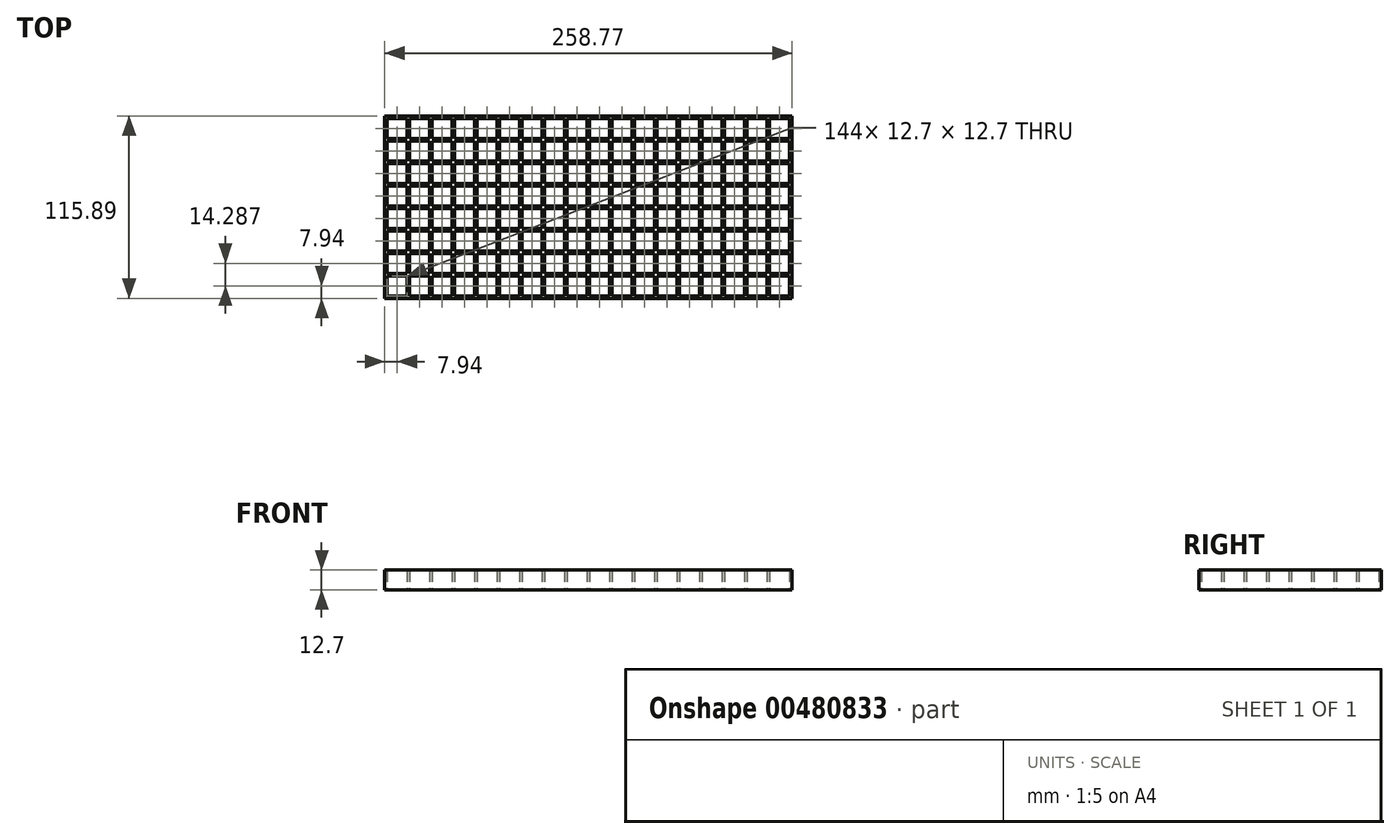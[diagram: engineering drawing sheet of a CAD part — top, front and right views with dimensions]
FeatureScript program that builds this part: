
annotation { "Feature Type Name" : "Feature", "Feature Type Description" : "" }
export const myFeature = defineFeature(function(context is Context, id is Id, definition is map)
    precondition{}
    {
        {
            var Q0;
            Q0=qCreatedBy(makeId("Top.planeOp"),FACE);
            var sketch = newSketch(context, id + "F0", { "sketchPlane" : qUnion([Q0])});
            skLineSegment(sketch, "E0.bottom", {"start": v(0, 0) * mm, "end": v(12.7, 0) * mm});
            skLineSegment(sketch, "E0.top", {"start": v(0, 12.7) * mm, "end": v(12.7, 12.7) * mm});
            skLineSegment(sketch, "E0.left", {"start": v(0, 0) * mm, "end": v(0, 12.7) * mm});
            skLineSegment(sketch, "E0.right", {"start": v(12.7, 0) * mm, "end": v(12.7, 12.7) * mm});
            skLineSegment(sketch, "E1.0.1.0", {"start": v(0, 14.29) * mm, "end": v(12.7, 14.29) * mm});
            skLineSegment(sketch, "E1.0.1.1", {"start": v(0, 26.99) * mm, "end": v(12.7, 26.99) * mm});
            skLineSegment(sketch, "E1.0.1.2", {"start": v(0, 14.29) * mm, "end": v(0, 26.99) * mm});
            skLineSegment(sketch, "E1.0.1.3", {"start": v(12.7, 14.29) * mm, "end": v(12.7, 26.99) * mm});
            skLineSegment(sketch, "E1.0.2.0", {"start": v(0, 28.58) * mm, "end": v(12.7, 28.58) * mm});
            skLineSegment(sketch, "E1.0.2.1", {"start": v(0, 41.28) * mm, "end": v(12.7, 41.28) * mm});
            skLineSegment(sketch, "E1.0.2.2", {"start": v(0, 28.57) * mm, "end": v(0, 41.27) * mm});
            skLineSegment(sketch, "E1.0.2.3", {"start": v(12.7, 28.57) * mm, "end": v(12.7, 41.27) * mm});
            skLineSegment(sketch, "E1.0.3.0", {"start": v(0, 42.86) * mm, "end": v(12.7, 42.86) * mm});
            skLineSegment(sketch, "E1.0.3.1", {"start": v(0, 55.56) * mm, "end": v(12.7, 55.56) * mm});
            skLineSegment(sketch, "E1.0.3.2", {"start": v(0, 42.86) * mm, "end": v(0, 55.56) * mm});
            skLineSegment(sketch, "E1.0.3.3", {"start": v(12.7, 42.86) * mm, "end": v(12.7, 55.56) * mm});
            skLineSegment(sketch, "E1.0.4.0", {"start": v(0, 57.15) * mm, "end": v(12.7, 57.15) * mm});
            skLineSegment(sketch, "E1.0.4.1", {"start": v(0, 69.85) * mm, "end": v(12.7, 69.85) * mm});
            skLineSegment(sketch, "E1.0.4.2", {"start": v(0, 57.15) * mm, "end": v(0, 69.85) * mm});
            skLineSegment(sketch, "E1.0.4.3", {"start": v(12.7, 57.15) * mm, "end": v(12.7, 69.85) * mm});
            skLineSegment(sketch, "E1.0.5.0", {"start": v(0, 71.44) * mm, "end": v(12.7, 71.44) * mm});
            skLineSegment(sketch, "E1.0.5.1", {"start": v(0, 84.14) * mm, "end": v(12.7, 84.14) * mm});
            skLineSegment(sketch, "E1.0.5.2", {"start": v(0, 71.44) * mm, "end": v(0, 84.14) * mm});
            skLineSegment(sketch, "E1.0.5.3", {"start": v(12.7, 71.44) * mm, "end": v(12.7, 84.14) * mm});
            skLineSegment(sketch, "E1.0.6.0", {"start": v(0, 85.73) * mm, "end": v(12.7, 85.73) * mm});
            skLineSegment(sketch, "E1.0.6.1", {"start": v(0, 98.43) * mm, "end": v(12.7, 98.43) * mm});
            skLineSegment(sketch, "E1.0.6.2", {"start": v(0, 85.73) * mm, "end": v(0, 98.43) * mm});
            skLineSegment(sketch, "E1.0.6.3", {"start": v(12.7, 85.73) * mm, "end": v(12.7, 98.43) * mm});
            skLineSegment(sketch, "E1.0.7.0", {"start": v(0, 100.01) * mm, "end": v(12.7, 100.01) * mm});
            skLineSegment(sketch, "E1.0.7.1", {"start": v(0, 112.71) * mm, "end": v(12.7, 112.71) * mm});
            skLineSegment(sketch, "E1.0.7.2", {"start": v(0, 100.01) * mm, "end": v(0, 112.71) * mm});
            skLineSegment(sketch, "E1.0.7.3", {"start": v(12.7, 100.01) * mm, "end": v(12.7, 112.71) * mm});
            skLineSegment(sketch, "E1.1.0.0", {"start": v(14.29, 0) * mm, "end": v(26.99, 0) * mm});
            skLineSegment(sketch, "E1.1.0.1", {"start": v(14.29, 12.7) * mm, "end": v(26.99, 12.7) * mm});
            skLineSegment(sketch, "E1.1.0.2", {"start": v(14.29, 0) * mm, "end": v(14.29, 12.7) * mm});
            skLineSegment(sketch, "E1.1.0.3", {"start": v(26.99, 0) * mm, "end": v(26.99, 12.7) * mm});
            skLineSegment(sketch, "E1.1.1.0", {"start": v(14.29, 14.29) * mm, "end": v(26.99, 14.29) * mm});
            skLineSegment(sketch, "E1.1.1.1", {"start": v(14.29, 26.99) * mm, "end": v(26.99, 26.99) * mm});
            skLineSegment(sketch, "E1.1.1.2", {"start": v(14.29, 14.29) * mm, "end": v(14.29, 26.99) * mm});
            skLineSegment(sketch, "E1.1.1.3", {"start": v(26.99, 14.29) * mm, "end": v(26.99, 26.99) * mm});
            skLineSegment(sketch, "E1.1.2.0", {"start": v(14.29, 28.58) * mm, "end": v(26.99, 28.58) * mm});
            skLineSegment(sketch, "E1.1.2.1", {"start": v(14.29, 41.28) * mm, "end": v(26.99, 41.28) * mm});
            skLineSegment(sketch, "E1.1.2.2", {"start": v(14.29, 28.57) * mm, "end": v(14.29, 41.27) * mm});
            skLineSegment(sketch, "E1.1.2.3", {"start": v(26.99, 28.57) * mm, "end": v(26.99, 41.27) * mm});
            skLineSegment(sketch, "E1.1.3.0", {"start": v(14.29, 42.86) * mm, "end": v(26.99, 42.86) * mm});
            skLineSegment(sketch, "E1.1.3.1", {"start": v(14.29, 55.56) * mm, "end": v(26.99, 55.56) * mm});
            skLineSegment(sketch, "E1.1.3.2", {"start": v(14.29, 42.86) * mm, "end": v(14.29, 55.56) * mm});
            skLineSegment(sketch, "E1.1.3.3", {"start": v(26.99, 42.86) * mm, "end": v(26.99, 55.56) * mm});
            skLineSegment(sketch, "E1.1.4.0", {"start": v(14.29, 57.15) * mm, "end": v(26.99, 57.15) * mm});
            skLineSegment(sketch, "E1.1.4.1", {"start": v(14.29, 69.85) * mm, "end": v(26.99, 69.85) * mm});
            skLineSegment(sketch, "E1.1.4.2", {"start": v(14.29, 57.15) * mm, "end": v(14.29, 69.85) * mm});
            skLineSegment(sketch, "E1.1.4.3", {"start": v(26.99, 57.15) * mm, "end": v(26.99, 69.85) * mm});
            skLineSegment(sketch, "E1.1.5.0", {"start": v(14.29, 71.44) * mm, "end": v(26.99, 71.44) * mm});
            skLineSegment(sketch, "E1.1.5.1", {"start": v(14.29, 84.14) * mm, "end": v(26.99, 84.14) * mm});
            skLineSegment(sketch, "E1.1.5.2", {"start": v(14.29, 71.44) * mm, "end": v(14.29, 84.14) * mm});
            skLineSegment(sketch, "E1.1.5.3", {"start": v(26.99, 71.44) * mm, "end": v(26.99, 84.14) * mm});
            skLineSegment(sketch, "E1.1.6.0", {"start": v(14.29, 85.73) * mm, "end": v(26.99, 85.73) * mm});
            skLineSegment(sketch, "E1.1.6.1", {"start": v(14.29, 98.43) * mm, "end": v(26.99, 98.43) * mm});
            skLineSegment(sketch, "E1.1.6.2", {"start": v(14.29, 85.73) * mm, "end": v(14.29, 98.43) * mm});
            skLineSegment(sketch, "E1.1.6.3", {"start": v(26.99, 85.73) * mm, "end": v(26.99, 98.43) * mm});
            skLineSegment(sketch, "E1.1.7.0", {"start": v(14.29, 100.01) * mm, "end": v(26.99, 100.01) * mm});
            skLineSegment(sketch, "E1.1.7.1", {"start": v(14.29, 112.71) * mm, "end": v(26.99, 112.71) * mm});
            skLineSegment(sketch, "E1.1.7.2", {"start": v(14.29, 100.01) * mm, "end": v(14.29, 112.71) * mm});
            skLineSegment(sketch, "E1.1.7.3", {"start": v(26.99, 100.01) * mm, "end": v(26.99, 112.71) * mm});
            skLineSegment(sketch, "E1.2.0.0", {"start": v(28.58, 0) * mm, "end": v(41.28, 0) * mm});
            skLineSegment(sketch, "E1.2.0.1", {"start": v(28.58, 12.7) * mm, "end": v(41.27, 12.7) * mm});
            skLineSegment(sketch, "E1.2.0.2", {"start": v(28.58, 0) * mm, "end": v(28.58, 12.7) * mm});
            skLineSegment(sketch, "E1.2.0.3", {"start": v(41.28, 0) * mm, "end": v(41.28, 12.7) * mm});
            skLineSegment(sketch, "E1.2.1.0", {"start": v(28.58, 14.29) * mm, "end": v(41.28, 14.29) * mm});
            skLineSegment(sketch, "E1.2.1.1", {"start": v(28.58, 26.99) * mm, "end": v(41.27, 26.99) * mm});
            skLineSegment(sketch, "E1.2.1.2", {"start": v(28.58, 14.29) * mm, "end": v(28.58, 26.99) * mm});
            skLineSegment(sketch, "E1.2.1.3", {"start": v(41.28, 14.29) * mm, "end": v(41.28, 26.99) * mm});
            skLineSegment(sketch, "E1.2.2.0", {"start": v(28.58, 28.58) * mm, "end": v(41.28, 28.58) * mm});
            skLineSegment(sketch, "E1.2.2.1", {"start": v(28.58, 41.28) * mm, "end": v(41.27, 41.28) * mm});
            skLineSegment(sketch, "E1.2.2.2", {"start": v(28.58, 28.57) * mm, "end": v(28.58, 41.27) * mm});
            skLineSegment(sketch, "E1.2.2.3", {"start": v(41.28, 28.57) * mm, "end": v(41.28, 41.27) * mm});
            skLineSegment(sketch, "E1.2.3.0", {"start": v(28.58, 42.86) * mm, "end": v(41.28, 42.86) * mm});
            skLineSegment(sketch, "E1.2.3.1", {"start": v(28.58, 55.56) * mm, "end": v(41.27, 55.56) * mm});
            skLineSegment(sketch, "E1.2.3.2", {"start": v(28.58, 42.86) * mm, "end": v(28.58, 55.56) * mm});
            skLineSegment(sketch, "E1.2.3.3", {"start": v(41.28, 42.86) * mm, "end": v(41.28, 55.56) * mm});
            skLineSegment(sketch, "E1.2.4.0", {"start": v(28.58, 57.15) * mm, "end": v(41.28, 57.15) * mm});
            skLineSegment(sketch, "E1.2.4.1", {"start": v(28.58, 69.85) * mm, "end": v(41.27, 69.85) * mm});
            skLineSegment(sketch, "E1.2.4.2", {"start": v(28.58, 57.15) * mm, "end": v(28.58, 69.85) * mm});
            skLineSegment(sketch, "E1.2.4.3", {"start": v(41.28, 57.15) * mm, "end": v(41.28, 69.85) * mm});
            skLineSegment(sketch, "E1.2.5.0", {"start": v(28.58, 71.44) * mm, "end": v(41.28, 71.44) * mm});
            skLineSegment(sketch, "E1.2.5.1", {"start": v(28.58, 84.14) * mm, "end": v(41.27, 84.14) * mm});
            skLineSegment(sketch, "E1.2.5.2", {"start": v(28.58, 71.44) * mm, "end": v(28.58, 84.14) * mm});
            skLineSegment(sketch, "E1.2.5.3", {"start": v(41.28, 71.44) * mm, "end": v(41.28, 84.14) * mm});
            skLineSegment(sketch, "E1.2.6.0", {"start": v(28.58, 85.73) * mm, "end": v(41.28, 85.73) * mm});
            skLineSegment(sketch, "E1.2.6.1", {"start": v(28.58, 98.43) * mm, "end": v(41.27, 98.43) * mm});
            skLineSegment(sketch, "E1.2.6.2", {"start": v(28.58, 85.73) * mm, "end": v(28.58, 98.43) * mm});
            skLineSegment(sketch, "E1.2.6.3", {"start": v(41.28, 85.73) * mm, "end": v(41.28, 98.43) * mm});
            skLineSegment(sketch, "E1.2.7.0", {"start": v(28.58, 100.01) * mm, "end": v(41.28, 100.01) * mm});
            skLineSegment(sketch, "E1.2.7.1", {"start": v(28.58, 112.71) * mm, "end": v(41.27, 112.71) * mm});
            skLineSegment(sketch, "E1.2.7.2", {"start": v(28.58, 100.01) * mm, "end": v(28.58, 112.71) * mm});
            skLineSegment(sketch, "E1.2.7.3", {"start": v(41.28, 100.01) * mm, "end": v(41.28, 112.71) * mm});
            skLineSegment(sketch, "E1.3.0.0", {"start": v(42.86, 0) * mm, "end": v(55.56, 0) * mm});
            skLineSegment(sketch, "E1.3.0.1", {"start": v(42.86, 12.7) * mm, "end": v(55.56, 12.7) * mm});
            skLineSegment(sketch, "E1.3.0.2", {"start": v(42.86, 0) * mm, "end": v(42.86, 12.7) * mm});
            skLineSegment(sketch, "E1.3.0.3", {"start": v(55.56, 0) * mm, "end": v(55.56, 12.7) * mm});
            skLineSegment(sketch, "E1.3.1.0", {"start": v(42.86, 14.29) * mm, "end": v(55.56, 14.29) * mm});
            skLineSegment(sketch, "E1.3.1.1", {"start": v(42.86, 26.99) * mm, "end": v(55.56, 26.99) * mm});
            skLineSegment(sketch, "E1.3.1.2", {"start": v(42.86, 14.29) * mm, "end": v(42.86, 26.99) * mm});
            skLineSegment(sketch, "E1.3.1.3", {"start": v(55.56, 14.29) * mm, "end": v(55.56, 26.99) * mm});
            skLineSegment(sketch, "E1.3.2.0", {"start": v(42.86, 28.58) * mm, "end": v(55.56, 28.58) * mm});
            skLineSegment(sketch, "E1.3.2.1", {"start": v(42.86, 41.28) * mm, "end": v(55.56, 41.28) * mm});
            skLineSegment(sketch, "E1.3.2.2", {"start": v(42.86, 28.57) * mm, "end": v(42.86, 41.27) * mm});
            skLineSegment(sketch, "E1.3.2.3", {"start": v(55.56, 28.57) * mm, "end": v(55.56, 41.27) * mm});
            skLineSegment(sketch, "E1.3.3.0", {"start": v(42.86, 42.86) * mm, "end": v(55.56, 42.86) * mm});
            skLineSegment(sketch, "E1.3.3.1", {"start": v(42.86, 55.56) * mm, "end": v(55.56, 55.56) * mm});
            skLineSegment(sketch, "E1.3.3.2", {"start": v(42.86, 42.86) * mm, "end": v(42.86, 55.56) * mm});
            skLineSegment(sketch, "E1.3.3.3", {"start": v(55.56, 42.86) * mm, "end": v(55.56, 55.56) * mm});
            skLineSegment(sketch, "E1.3.4.0", {"start": v(42.86, 57.15) * mm, "end": v(55.56, 57.15) * mm});
            skLineSegment(sketch, "E1.3.4.1", {"start": v(42.86, 69.85) * mm, "end": v(55.56, 69.85) * mm});
            skLineSegment(sketch, "E1.3.4.2", {"start": v(42.86, 57.15) * mm, "end": v(42.86, 69.85) * mm});
            skLineSegment(sketch, "E1.3.4.3", {"start": v(55.56, 57.15) * mm, "end": v(55.56, 69.85) * mm});
            skLineSegment(sketch, "E1.3.5.0", {"start": v(42.86, 71.44) * mm, "end": v(55.56, 71.44) * mm});
            skLineSegment(sketch, "E1.3.5.1", {"start": v(42.86, 84.14) * mm, "end": v(55.56, 84.14) * mm});
            skLineSegment(sketch, "E1.3.5.2", {"start": v(42.86, 71.44) * mm, "end": v(42.86, 84.14) * mm});
            skLineSegment(sketch, "E1.3.5.3", {"start": v(55.56, 71.44) * mm, "end": v(55.56, 84.14) * mm});
            skLineSegment(sketch, "E1.3.6.0", {"start": v(42.86, 85.73) * mm, "end": v(55.56, 85.73) * mm});
            skLineSegment(sketch, "E1.3.6.1", {"start": v(42.86, 98.43) * mm, "end": v(55.56, 98.43) * mm});
            skLineSegment(sketch, "E1.3.6.2", {"start": v(42.86, 85.73) * mm, "end": v(42.86, 98.43) * mm});
            skLineSegment(sketch, "E1.3.6.3", {"start": v(55.56, 85.73) * mm, "end": v(55.56, 98.43) * mm});
            skLineSegment(sketch, "E1.3.7.0", {"start": v(42.86, 100.01) * mm, "end": v(55.56, 100.01) * mm});
            skLineSegment(sketch, "E1.3.7.1", {"start": v(42.86, 112.71) * mm, "end": v(55.56, 112.71) * mm});
            skLineSegment(sketch, "E1.3.7.2", {"start": v(42.86, 100.01) * mm, "end": v(42.86, 112.71) * mm});
            skLineSegment(sketch, "E1.3.7.3", {"start": v(55.56, 100.01) * mm, "end": v(55.56, 112.71) * mm});
            skLineSegment(sketch, "E1.4.0.0", {"start": v(57.15, 0) * mm, "end": v(69.85, 0) * mm});
            skLineSegment(sketch, "E1.4.0.1", {"start": v(57.15, 12.7) * mm, "end": v(69.85, 12.7) * mm});
            skLineSegment(sketch, "E1.4.0.2", {"start": v(57.15, 0) * mm, "end": v(57.15, 12.7) * mm});
            skLineSegment(sketch, "E1.4.0.3", {"start": v(69.85, 0) * mm, "end": v(69.85, 12.7) * mm});
            skLineSegment(sketch, "E1.4.1.0", {"start": v(57.15, 14.29) * mm, "end": v(69.85, 14.29) * mm});
            skLineSegment(sketch, "E1.4.1.1", {"start": v(57.15, 26.99) * mm, "end": v(69.85, 26.99) * mm});
            skLineSegment(sketch, "E1.4.1.2", {"start": v(57.15, 14.29) * mm, "end": v(57.15, 26.99) * mm});
            skLineSegment(sketch, "E1.4.1.3", {"start": v(69.85, 14.29) * mm, "end": v(69.85, 26.99) * mm});
            skLineSegment(sketch, "E1.4.2.0", {"start": v(57.15, 28.58) * mm, "end": v(69.85, 28.58) * mm});
            skLineSegment(sketch, "E1.4.2.1", {"start": v(57.15, 41.28) * mm, "end": v(69.85, 41.28) * mm});
            skLineSegment(sketch, "E1.4.2.2", {"start": v(57.15, 28.57) * mm, "end": v(57.15, 41.27) * mm});
            skLineSegment(sketch, "E1.4.2.3", {"start": v(69.85, 28.57) * mm, "end": v(69.85, 41.27) * mm});
            skLineSegment(sketch, "E1.4.3.0", {"start": v(57.15, 42.86) * mm, "end": v(69.85, 42.86) * mm});
            skLineSegment(sketch, "E1.4.3.1", {"start": v(57.15, 55.56) * mm, "end": v(69.85, 55.56) * mm});
            skLineSegment(sketch, "E1.4.3.2", {"start": v(57.15, 42.86) * mm, "end": v(57.15, 55.56) * mm});
            skLineSegment(sketch, "E1.4.3.3", {"start": v(69.85, 42.86) * mm, "end": v(69.85, 55.56) * mm});
            skLineSegment(sketch, "E1.4.4.0", {"start": v(57.15, 57.15) * mm, "end": v(69.85, 57.15) * mm});
            skLineSegment(sketch, "E1.4.4.1", {"start": v(57.15, 69.85) * mm, "end": v(69.85, 69.85) * mm});
            skLineSegment(sketch, "E1.4.4.2", {"start": v(57.15, 57.15) * mm, "end": v(57.15, 69.85) * mm});
            skLineSegment(sketch, "E1.4.4.3", {"start": v(69.85, 57.15) * mm, "end": v(69.85, 69.85) * mm});
            skLineSegment(sketch, "E1.4.5.0", {"start": v(57.15, 71.44) * mm, "end": v(69.85, 71.44) * mm});
            skLineSegment(sketch, "E1.4.5.1", {"start": v(57.15, 84.14) * mm, "end": v(69.85, 84.14) * mm});
            skLineSegment(sketch, "E1.4.5.2", {"start": v(57.15, 71.44) * mm, "end": v(57.15, 84.14) * mm});
            skLineSegment(sketch, "E1.4.5.3", {"start": v(69.85, 71.44) * mm, "end": v(69.85, 84.14) * mm});
            skLineSegment(sketch, "E1.4.6.0", {"start": v(57.15, 85.73) * mm, "end": v(69.85, 85.73) * mm});
            skLineSegment(sketch, "E1.4.6.1", {"start": v(57.15, 98.43) * mm, "end": v(69.85, 98.43) * mm});
            skLineSegment(sketch, "E1.4.6.2", {"start": v(57.15, 85.73) * mm, "end": v(57.15, 98.43) * mm});
            skLineSegment(sketch, "E1.4.6.3", {"start": v(69.85, 85.73) * mm, "end": v(69.85, 98.43) * mm});
            skLineSegment(sketch, "E1.4.7.0", {"start": v(57.15, 100.01) * mm, "end": v(69.85, 100.01) * mm});
            skLineSegment(sketch, "E1.4.7.1", {"start": v(57.15, 112.71) * mm, "end": v(69.85, 112.71) * mm});
            skLineSegment(sketch, "E1.4.7.2", {"start": v(57.15, 100.01) * mm, "end": v(57.15, 112.71) * mm});
            skLineSegment(sketch, "E1.4.7.3", {"start": v(69.85, 100.01) * mm, "end": v(69.85, 112.71) * mm});
            skLineSegment(sketch, "E1.5.0.0", {"start": v(71.44, 0) * mm, "end": v(84.14, 0) * mm});
            skLineSegment(sketch, "E1.5.0.1", {"start": v(71.44, 12.7) * mm, "end": v(84.14, 12.7) * mm});
            skLineSegment(sketch, "E1.5.0.2", {"start": v(71.44, 0) * mm, "end": v(71.44, 12.7) * mm});
            skLineSegment(sketch, "E1.5.0.3", {"start": v(84.14, 0) * mm, "end": v(84.14, 12.7) * mm});
            skLineSegment(sketch, "E1.5.1.0", {"start": v(71.44, 14.29) * mm, "end": v(84.14, 14.29) * mm});
            skLineSegment(sketch, "E1.5.1.1", {"start": v(71.44, 26.99) * mm, "end": v(84.14, 26.99) * mm});
            skLineSegment(sketch, "E1.5.1.2", {"start": v(71.44, 14.29) * mm, "end": v(71.44, 26.99) * mm});
            skLineSegment(sketch, "E1.5.1.3", {"start": v(84.14, 14.29) * mm, "end": v(84.14, 26.99) * mm});
            skLineSegment(sketch, "E1.5.2.0", {"start": v(71.44, 28.58) * mm, "end": v(84.14, 28.58) * mm});
            skLineSegment(sketch, "E1.5.2.1", {"start": v(71.44, 41.28) * mm, "end": v(84.14, 41.28) * mm});
            skLineSegment(sketch, "E1.5.2.2", {"start": v(71.44, 28.57) * mm, "end": v(71.44, 41.27) * mm});
            skLineSegment(sketch, "E1.5.2.3", {"start": v(84.14, 28.57) * mm, "end": v(84.14, 41.27) * mm});
            skLineSegment(sketch, "E1.5.3.0", {"start": v(71.44, 42.86) * mm, "end": v(84.14, 42.86) * mm});
            skLineSegment(sketch, "E1.5.3.1", {"start": v(71.44, 55.56) * mm, "end": v(84.14, 55.56) * mm});
            skLineSegment(sketch, "E1.5.3.2", {"start": v(71.44, 42.86) * mm, "end": v(71.44, 55.56) * mm});
            skLineSegment(sketch, "E1.5.3.3", {"start": v(84.14, 42.86) * mm, "end": v(84.14, 55.56) * mm});
            skLineSegment(sketch, "E1.5.4.0", {"start": v(71.44, 57.15) * mm, "end": v(84.14, 57.15) * mm});
            skLineSegment(sketch, "E1.5.4.1", {"start": v(71.44, 69.85) * mm, "end": v(84.14, 69.85) * mm});
            skLineSegment(sketch, "E1.5.4.2", {"start": v(71.44, 57.15) * mm, "end": v(71.44, 69.85) * mm});
            skLineSegment(sketch, "E1.5.4.3", {"start": v(84.14, 57.15) * mm, "end": v(84.14, 69.85) * mm});
            skLineSegment(sketch, "E1.5.5.0", {"start": v(71.44, 71.44) * mm, "end": v(84.14, 71.44) * mm});
            skLineSegment(sketch, "E1.5.5.1", {"start": v(71.44, 84.14) * mm, "end": v(84.14, 84.14) * mm});
            skLineSegment(sketch, "E1.5.5.2", {"start": v(71.44, 71.44) * mm, "end": v(71.44, 84.14) * mm});
            skLineSegment(sketch, "E1.5.5.3", {"start": v(84.14, 71.44) * mm, "end": v(84.14, 84.14) * mm});
            skLineSegment(sketch, "E1.5.6.0", {"start": v(71.44, 85.73) * mm, "end": v(84.14, 85.73) * mm});
            skLineSegment(sketch, "E1.5.6.1", {"start": v(71.44, 98.43) * mm, "end": v(84.14, 98.43) * mm});
            skLineSegment(sketch, "E1.5.6.2", {"start": v(71.44, 85.73) * mm, "end": v(71.44, 98.43) * mm});
            skLineSegment(sketch, "E1.5.6.3", {"start": v(84.14, 85.73) * mm, "end": v(84.14, 98.43) * mm});
            skLineSegment(sketch, "E1.5.7.0", {"start": v(71.44, 100.01) * mm, "end": v(84.14, 100.01) * mm});
            skLineSegment(sketch, "E1.5.7.1", {"start": v(71.44, 112.71) * mm, "end": v(84.14, 112.71) * mm});
            skLineSegment(sketch, "E1.5.7.2", {"start": v(71.44, 100.01) * mm, "end": v(71.44, 112.71) * mm});
            skLineSegment(sketch, "E1.5.7.3", {"start": v(84.14, 100.01) * mm, "end": v(84.14, 112.71) * mm});
            skLineSegment(sketch, "E1.6.0.0", {"start": v(85.73, 0) * mm, "end": v(98.42, 0) * mm});
            skLineSegment(sketch, "E1.6.0.1", {"start": v(85.72, 12.7) * mm, "end": v(98.42, 12.7) * mm});
            skLineSegment(sketch, "E1.6.0.2", {"start": v(85.73, 0) * mm, "end": v(85.73, 12.7) * mm});
            skLineSegment(sketch, "E1.6.0.3", {"start": v(98.43, 0) * mm, "end": v(98.43, 12.7) * mm});
            skLineSegment(sketch, "E1.6.1.0", {"start": v(85.73, 14.29) * mm, "end": v(98.42, 14.29) * mm});
            skLineSegment(sketch, "E1.6.1.1", {"start": v(85.72, 26.99) * mm, "end": v(98.42, 26.99) * mm});
            skLineSegment(sketch, "E1.6.1.2", {"start": v(85.73, 14.29) * mm, "end": v(85.73, 26.99) * mm});
            skLineSegment(sketch, "E1.6.1.3", {"start": v(98.43, 14.29) * mm, "end": v(98.43, 26.99) * mm});
            skLineSegment(sketch, "E1.6.2.0", {"start": v(85.73, 28.58) * mm, "end": v(98.42, 28.58) * mm});
            skLineSegment(sketch, "E1.6.2.1", {"start": v(85.72, 41.28) * mm, "end": v(98.42, 41.28) * mm});
            skLineSegment(sketch, "E1.6.2.2", {"start": v(85.73, 28.57) * mm, "end": v(85.73, 41.27) * mm});
            skLineSegment(sketch, "E1.6.2.3", {"start": v(98.43, 28.57) * mm, "end": v(98.43, 41.27) * mm});
            skLineSegment(sketch, "E1.6.3.0", {"start": v(85.73, 42.86) * mm, "end": v(98.42, 42.86) * mm});
            skLineSegment(sketch, "E1.6.3.1", {"start": v(85.72, 55.56) * mm, "end": v(98.42, 55.56) * mm});
            skLineSegment(sketch, "E1.6.3.2", {"start": v(85.73, 42.86) * mm, "end": v(85.73, 55.56) * mm});
            skLineSegment(sketch, "E1.6.3.3", {"start": v(98.43, 42.86) * mm, "end": v(98.43, 55.56) * mm});
            skLineSegment(sketch, "E1.6.4.0", {"start": v(85.73, 57.15) * mm, "end": v(98.42, 57.15) * mm});
            skLineSegment(sketch, "E1.6.4.1", {"start": v(85.72, 69.85) * mm, "end": v(98.42, 69.85) * mm});
            skLineSegment(sketch, "E1.6.4.2", {"start": v(85.73, 57.15) * mm, "end": v(85.73, 69.85) * mm});
            skLineSegment(sketch, "E1.6.4.3", {"start": v(98.43, 57.15) * mm, "end": v(98.43, 69.85) * mm});
            skLineSegment(sketch, "E1.6.5.0", {"start": v(85.73, 71.44) * mm, "end": v(98.42, 71.44) * mm});
            skLineSegment(sketch, "E1.6.5.1", {"start": v(85.72, 84.14) * mm, "end": v(98.42, 84.14) * mm});
            skLineSegment(sketch, "E1.6.5.2", {"start": v(85.73, 71.44) * mm, "end": v(85.73, 84.14) * mm});
            skLineSegment(sketch, "E1.6.5.3", {"start": v(98.43, 71.44) * mm, "end": v(98.43, 84.14) * mm});
            skLineSegment(sketch, "E1.6.6.0", {"start": v(85.73, 85.73) * mm, "end": v(98.42, 85.73) * mm});
            skLineSegment(sketch, "E1.6.6.1", {"start": v(85.72, 98.43) * mm, "end": v(98.42, 98.43) * mm});
            skLineSegment(sketch, "E1.6.6.2", {"start": v(85.73, 85.73) * mm, "end": v(85.73, 98.43) * mm});
            skLineSegment(sketch, "E1.6.6.3", {"start": v(98.43, 85.73) * mm, "end": v(98.43, 98.43) * mm});
            skLineSegment(sketch, "E1.6.7.0", {"start": v(85.73, 100.01) * mm, "end": v(98.42, 100.01) * mm});
            skLineSegment(sketch, "E1.6.7.1", {"start": v(85.72, 112.71) * mm, "end": v(98.42, 112.71) * mm});
            skLineSegment(sketch, "E1.6.7.2", {"start": v(85.73, 100.01) * mm, "end": v(85.73, 112.71) * mm});
            skLineSegment(sketch, "E1.6.7.3", {"start": v(98.43, 100.01) * mm, "end": v(98.43, 112.71) * mm});
            skLineSegment(sketch, "E1.7.0.0", {"start": v(100.01, 0) * mm, "end": v(112.71, 0) * mm});
            skLineSegment(sketch, "E1.7.0.1", {"start": v(100.01, 12.7) * mm, "end": v(112.71, 12.7) * mm});
            skLineSegment(sketch, "E1.7.0.2", {"start": v(100.01, 0) * mm, "end": v(100.01, 12.7) * mm});
            skLineSegment(sketch, "E1.7.0.3", {"start": v(112.71, 0) * mm, "end": v(112.71, 12.7) * mm});
            skLineSegment(sketch, "E1.7.1.0", {"start": v(100.01, 14.29) * mm, "end": v(112.71, 14.29) * mm});
            skLineSegment(sketch, "E1.7.1.1", {"start": v(100.01, 26.99) * mm, "end": v(112.71, 26.99) * mm});
            skLineSegment(sketch, "E1.7.1.2", {"start": v(100.01, 14.29) * mm, "end": v(100.01, 26.99) * mm});
            skLineSegment(sketch, "E1.7.1.3", {"start": v(112.71, 14.29) * mm, "end": v(112.71, 26.99) * mm});
            skLineSegment(sketch, "E1.7.2.0", {"start": v(100.01, 28.58) * mm, "end": v(112.71, 28.58) * mm});
            skLineSegment(sketch, "E1.7.2.1", {"start": v(100.01, 41.28) * mm, "end": v(112.71, 41.28) * mm});
            skLineSegment(sketch, "E1.7.2.2", {"start": v(100.01, 28.57) * mm, "end": v(100.01, 41.27) * mm});
            skLineSegment(sketch, "E1.7.2.3", {"start": v(112.71, 28.57) * mm, "end": v(112.71, 41.27) * mm});
            skLineSegment(sketch, "E1.7.3.0", {"start": v(100.01, 42.86) * mm, "end": v(112.71, 42.86) * mm});
            skLineSegment(sketch, "E1.7.3.1", {"start": v(100.01, 55.56) * mm, "end": v(112.71, 55.56) * mm});
            skLineSegment(sketch, "E1.7.3.2", {"start": v(100.01, 42.86) * mm, "end": v(100.01, 55.56) * mm});
            skLineSegment(sketch, "E1.7.3.3", {"start": v(112.71, 42.86) * mm, "end": v(112.71, 55.56) * mm});
            skLineSegment(sketch, "E1.7.4.0", {"start": v(100.01, 57.15) * mm, "end": v(112.71, 57.15) * mm});
            skLineSegment(sketch, "E1.7.4.1", {"start": v(100.01, 69.85) * mm, "end": v(112.71, 69.85) * mm});
            skLineSegment(sketch, "E1.7.4.2", {"start": v(100.01, 57.15) * mm, "end": v(100.01, 69.85) * mm});
            skLineSegment(sketch, "E1.7.4.3", {"start": v(112.71, 57.15) * mm, "end": v(112.71, 69.85) * mm});
            skLineSegment(sketch, "E1.7.5.0", {"start": v(100.01, 71.44) * mm, "end": v(112.71, 71.44) * mm});
            skLineSegment(sketch, "E1.7.5.1", {"start": v(100.01, 84.14) * mm, "end": v(112.71, 84.14) * mm});
            skLineSegment(sketch, "E1.7.5.2", {"start": v(100.01, 71.44) * mm, "end": v(100.01, 84.14) * mm});
            skLineSegment(sketch, "E1.7.5.3", {"start": v(112.71, 71.44) * mm, "end": v(112.71, 84.14) * mm});
            skLineSegment(sketch, "E1.7.6.0", {"start": v(100.01, 85.73) * mm, "end": v(112.71, 85.73) * mm});
            skLineSegment(sketch, "E1.7.6.1", {"start": v(100.01, 98.43) * mm, "end": v(112.71, 98.43) * mm});
            skLineSegment(sketch, "E1.7.6.2", {"start": v(100.01, 85.73) * mm, "end": v(100.01, 98.43) * mm});
            skLineSegment(sketch, "E1.7.6.3", {"start": v(112.71, 85.73) * mm, "end": v(112.71, 98.43) * mm});
            skLineSegment(sketch, "E1.7.7.0", {"start": v(100.01, 100.01) * mm, "end": v(112.71, 100.01) * mm});
            skLineSegment(sketch, "E1.7.7.1", {"start": v(100.01, 112.71) * mm, "end": v(112.71, 112.71) * mm});
            skLineSegment(sketch, "E1.7.7.2", {"start": v(100.01, 100.01) * mm, "end": v(100.01, 112.71) * mm});
            skLineSegment(sketch, "E1.7.7.3", {"start": v(112.71, 100.01) * mm, "end": v(112.71, 112.71) * mm});
            skLineSegment(sketch, "E1.8.0.0", {"start": v(114.3, 0) * mm, "end": v(127, 0) * mm});
            skLineSegment(sketch, "E1.8.0.1", {"start": v(114.3, 12.7) * mm, "end": v(127, 12.7) * mm});
            skLineSegment(sketch, "E1.8.0.2", {"start": v(114.3, 0) * mm, "end": v(114.3, 12.7) * mm});
            skLineSegment(sketch, "E1.8.0.3", {"start": v(127, 0) * mm, "end": v(127, 12.7) * mm});
            skLineSegment(sketch, "E1.8.1.0", {"start": v(114.3, 14.29) * mm, "end": v(127, 14.29) * mm});
            skLineSegment(sketch, "E1.8.1.1", {"start": v(114.3, 26.99) * mm, "end": v(127, 26.99) * mm});
            skLineSegment(sketch, "E1.8.1.2", {"start": v(114.3, 14.29) * mm, "end": v(114.3, 26.99) * mm});
            skLineSegment(sketch, "E1.8.1.3", {"start": v(127, 14.29) * mm, "end": v(127, 26.99) * mm});
            skLineSegment(sketch, "E1.8.2.0", {"start": v(114.3, 28.58) * mm, "end": v(127, 28.58) * mm});
            skLineSegment(sketch, "E1.8.2.1", {"start": v(114.3, 41.28) * mm, "end": v(127, 41.28) * mm});
            skLineSegment(sketch, "E1.8.2.2", {"start": v(114.3, 28.57) * mm, "end": v(114.3, 41.27) * mm});
            skLineSegment(sketch, "E1.8.2.3", {"start": v(127, 28.57) * mm, "end": v(127, 41.27) * mm});
            skLineSegment(sketch, "E1.8.3.0", {"start": v(114.3, 42.86) * mm, "end": v(127, 42.86) * mm});
            skLineSegment(sketch, "E1.8.3.1", {"start": v(114.3, 55.56) * mm, "end": v(127, 55.56) * mm});
            skLineSegment(sketch, "E1.8.3.2", {"start": v(114.3, 42.86) * mm, "end": v(114.3, 55.56) * mm});
            skLineSegment(sketch, "E1.8.3.3", {"start": v(127, 42.86) * mm, "end": v(127, 55.56) * mm});
            skLineSegment(sketch, "E1.8.4.0", {"start": v(114.3, 57.15) * mm, "end": v(127, 57.15) * mm});
            skLineSegment(sketch, "E1.8.4.1", {"start": v(114.3, 69.85) * mm, "end": v(127, 69.85) * mm});
            skLineSegment(sketch, "E1.8.4.2", {"start": v(114.3, 57.15) * mm, "end": v(114.3, 69.85) * mm});
            skLineSegment(sketch, "E1.8.4.3", {"start": v(127, 57.15) * mm, "end": v(127, 69.85) * mm});
            skLineSegment(sketch, "E1.8.5.0", {"start": v(114.3, 71.44) * mm, "end": v(127, 71.44) * mm});
            skLineSegment(sketch, "E1.8.5.1", {"start": v(114.3, 84.14) * mm, "end": v(127, 84.14) * mm});
            skLineSegment(sketch, "E1.8.5.2", {"start": v(114.3, 71.44) * mm, "end": v(114.3, 84.14) * mm});
            skLineSegment(sketch, "E1.8.5.3", {"start": v(127, 71.44) * mm, "end": v(127, 84.14) * mm});
            skLineSegment(sketch, "E1.8.6.0", {"start": v(114.3, 85.73) * mm, "end": v(127, 85.73) * mm});
            skLineSegment(sketch, "E1.8.6.1", {"start": v(114.3, 98.43) * mm, "end": v(127, 98.43) * mm});
            skLineSegment(sketch, "E1.8.6.2", {"start": v(114.3, 85.73) * mm, "end": v(114.3, 98.43) * mm});
            skLineSegment(sketch, "E1.8.6.3", {"start": v(127, 85.73) * mm, "end": v(127, 98.43) * mm});
            skLineSegment(sketch, "E1.8.7.0", {"start": v(114.3, 100.01) * mm, "end": v(127, 100.01) * mm});
            skLineSegment(sketch, "E1.8.7.1", {"start": v(114.3, 112.71) * mm, "end": v(127, 112.71) * mm});
            skLineSegment(sketch, "E1.8.7.2", {"start": v(114.3, 100.01) * mm, "end": v(114.3, 112.71) * mm});
            skLineSegment(sketch, "E1.8.7.3", {"start": v(127, 100.01) * mm, "end": v(127, 112.71) * mm});
            skLineSegment(sketch, "E1.9.0.0", {"start": v(128.59, 0) * mm, "end": v(141.29, 0) * mm});
            skLineSegment(sketch, "E1.9.0.1", {"start": v(128.59, 12.7) * mm, "end": v(141.29, 12.7) * mm});
            skLineSegment(sketch, "E1.9.0.2", {"start": v(128.59, 0) * mm, "end": v(128.59, 12.7) * mm});
            skLineSegment(sketch, "E1.9.0.3", {"start": v(141.29, 0) * mm, "end": v(141.29, 12.7) * mm});
            skLineSegment(sketch, "E1.9.1.0", {"start": v(128.59, 14.29) * mm, "end": v(141.29, 14.29) * mm});
            skLineSegment(sketch, "E1.9.1.1", {"start": v(128.59, 26.99) * mm, "end": v(141.29, 26.99) * mm});
            skLineSegment(sketch, "E1.9.1.2", {"start": v(128.59, 14.29) * mm, "end": v(128.59, 26.99) * mm});
            skLineSegment(sketch, "E1.9.1.3", {"start": v(141.29, 14.29) * mm, "end": v(141.29, 26.99) * mm});
            skLineSegment(sketch, "E1.9.2.0", {"start": v(128.59, 28.58) * mm, "end": v(141.29, 28.58) * mm});
            skLineSegment(sketch, "E1.9.2.1", {"start": v(128.59, 41.28) * mm, "end": v(141.29, 41.28) * mm});
            skLineSegment(sketch, "E1.9.2.2", {"start": v(128.59, 28.57) * mm, "end": v(128.59, 41.27) * mm});
            skLineSegment(sketch, "E1.9.2.3", {"start": v(141.29, 28.57) * mm, "end": v(141.29, 41.27) * mm});
            skLineSegment(sketch, "E1.9.3.0", {"start": v(128.59, 42.86) * mm, "end": v(141.29, 42.86) * mm});
            skLineSegment(sketch, "E1.9.3.1", {"start": v(128.59, 55.56) * mm, "end": v(141.29, 55.56) * mm});
            skLineSegment(sketch, "E1.9.3.2", {"start": v(128.59, 42.86) * mm, "end": v(128.59, 55.56) * mm});
            skLineSegment(sketch, "E1.9.3.3", {"start": v(141.29, 42.86) * mm, "end": v(141.29, 55.56) * mm});
            skLineSegment(sketch, "E1.9.4.0", {"start": v(128.59, 57.15) * mm, "end": v(141.29, 57.15) * mm});
            skLineSegment(sketch, "E1.9.4.1", {"start": v(128.59, 69.85) * mm, "end": v(141.29, 69.85) * mm});
            skLineSegment(sketch, "E1.9.4.2", {"start": v(128.59, 57.15) * mm, "end": v(128.59, 69.85) * mm});
            skLineSegment(sketch, "E1.9.4.3", {"start": v(141.29, 57.15) * mm, "end": v(141.29, 69.85) * mm});
            skLineSegment(sketch, "E1.9.5.0", {"start": v(128.59, 71.44) * mm, "end": v(141.29, 71.44) * mm});
            skLineSegment(sketch, "E1.9.5.1", {"start": v(128.59, 84.14) * mm, "end": v(141.29, 84.14) * mm});
            skLineSegment(sketch, "E1.9.5.2", {"start": v(128.59, 71.44) * mm, "end": v(128.59, 84.14) * mm});
            skLineSegment(sketch, "E1.9.5.3", {"start": v(141.29, 71.44) * mm, "end": v(141.29, 84.14) * mm});
            skLineSegment(sketch, "E1.9.6.0", {"start": v(128.59, 85.73) * mm, "end": v(141.29, 85.73) * mm});
            skLineSegment(sketch, "E1.9.6.1", {"start": v(128.59, 98.43) * mm, "end": v(141.29, 98.43) * mm});
            skLineSegment(sketch, "E1.9.6.2", {"start": v(128.59, 85.73) * mm, "end": v(128.59, 98.43) * mm});
            skLineSegment(sketch, "E1.9.6.3", {"start": v(141.29, 85.73) * mm, "end": v(141.29, 98.43) * mm});
            skLineSegment(sketch, "E1.9.7.0", {"start": v(128.59, 100.01) * mm, "end": v(141.29, 100.01) * mm});
            skLineSegment(sketch, "E1.9.7.1", {"start": v(128.59, 112.71) * mm, "end": v(141.29, 112.71) * mm});
            skLineSegment(sketch, "E1.9.7.2", {"start": v(128.59, 100.01) * mm, "end": v(128.59, 112.71) * mm});
            skLineSegment(sketch, "E1.9.7.3", {"start": v(141.29, 100.01) * mm, "end": v(141.29, 112.71) * mm});
            skLineSegment(sketch, "E1.10.0.0", {"start": v(142.88, 0) * mm, "end": v(155.58, 0) * mm});
            skLineSegment(sketch, "E1.10.0.1", {"start": v(142.88, 12.7) * mm, "end": v(155.58, 12.7) * mm});
            skLineSegment(sketch, "E1.10.0.2", {"start": v(142.88, 0) * mm, "end": v(142.88, 12.7) * mm});
            skLineSegment(sketch, "E1.10.0.3", {"start": v(155.58, 0) * mm, "end": v(155.58, 12.7) * mm});
            skLineSegment(sketch, "E1.10.1.0", {"start": v(142.88, 14.29) * mm, "end": v(155.58, 14.29) * mm});
            skLineSegment(sketch, "E1.10.1.1", {"start": v(142.88, 26.99) * mm, "end": v(155.58, 26.99) * mm});
            skLineSegment(sketch, "E1.10.1.2", {"start": v(142.88, 14.29) * mm, "end": v(142.88, 26.99) * mm});
            skLineSegment(sketch, "E1.10.1.3", {"start": v(155.58, 14.29) * mm, "end": v(155.58, 26.99) * mm});
            skLineSegment(sketch, "E1.10.2.0", {"start": v(142.88, 28.58) * mm, "end": v(155.58, 28.58) * mm});
            skLineSegment(sketch, "E1.10.2.1", {"start": v(142.88, 41.28) * mm, "end": v(155.58, 41.28) * mm});
            skLineSegment(sketch, "E1.10.2.2", {"start": v(142.88, 28.57) * mm, "end": v(142.88, 41.27) * mm});
            skLineSegment(sketch, "E1.10.2.3", {"start": v(155.58, 28.57) * mm, "end": v(155.58, 41.27) * mm});
            skLineSegment(sketch, "E1.10.3.0", {"start": v(142.88, 42.86) * mm, "end": v(155.58, 42.86) * mm});
            skLineSegment(sketch, "E1.10.3.1", {"start": v(142.88, 55.56) * mm, "end": v(155.58, 55.56) * mm});
            skLineSegment(sketch, "E1.10.3.2", {"start": v(142.88, 42.86) * mm, "end": v(142.88, 55.56) * mm});
            skLineSegment(sketch, "E1.10.3.3", {"start": v(155.58, 42.86) * mm, "end": v(155.58, 55.56) * mm});
            skLineSegment(sketch, "E1.10.4.0", {"start": v(142.88, 57.15) * mm, "end": v(155.58, 57.15) * mm});
            skLineSegment(sketch, "E1.10.4.1", {"start": v(142.88, 69.85) * mm, "end": v(155.58, 69.85) * mm});
            skLineSegment(sketch, "E1.10.4.2", {"start": v(142.88, 57.15) * mm, "end": v(142.88, 69.85) * mm});
            skLineSegment(sketch, "E1.10.4.3", {"start": v(155.58, 57.15) * mm, "end": v(155.58, 69.85) * mm});
            skLineSegment(sketch, "E1.10.5.0", {"start": v(142.88, 71.44) * mm, "end": v(155.58, 71.44) * mm});
            skLineSegment(sketch, "E1.10.5.1", {"start": v(142.88, 84.14) * mm, "end": v(155.58, 84.14) * mm});
            skLineSegment(sketch, "E1.10.5.2", {"start": v(142.88, 71.44) * mm, "end": v(142.88, 84.14) * mm});
            skLineSegment(sketch, "E1.10.5.3", {"start": v(155.58, 71.44) * mm, "end": v(155.58, 84.14) * mm});
            skLineSegment(sketch, "E1.10.6.0", {"start": v(142.88, 85.73) * mm, "end": v(155.58, 85.73) * mm});
            skLineSegment(sketch, "E1.10.6.1", {"start": v(142.88, 98.43) * mm, "end": v(155.58, 98.43) * mm});
            skLineSegment(sketch, "E1.10.6.2", {"start": v(142.88, 85.73) * mm, "end": v(142.88, 98.43) * mm});
            skLineSegment(sketch, "E1.10.6.3", {"start": v(155.58, 85.73) * mm, "end": v(155.58, 98.43) * mm});
            skLineSegment(sketch, "E1.10.7.0", {"start": v(142.88, 100.01) * mm, "end": v(155.58, 100.01) * mm});
            skLineSegment(sketch, "E1.10.7.1", {"start": v(142.88, 112.71) * mm, "end": v(155.58, 112.71) * mm});
            skLineSegment(sketch, "E1.10.7.2", {"start": v(142.88, 100.01) * mm, "end": v(142.88, 112.71) * mm});
            skLineSegment(sketch, "E1.10.7.3", {"start": v(155.58, 100.01) * mm, "end": v(155.58, 112.71) * mm});
            skLineSegment(sketch, "E1.11.0.0", {"start": v(157.16, 0) * mm, "end": v(169.86, 0) * mm});
            skLineSegment(sketch, "E1.11.0.1", {"start": v(157.16, 12.7) * mm, "end": v(169.86, 12.7) * mm});
            skLineSegment(sketch, "E1.11.0.2", {"start": v(157.16, 0) * mm, "end": v(157.16, 12.7) * mm});
            skLineSegment(sketch, "E1.11.0.3", {"start": v(169.86, 0) * mm, "end": v(169.86, 12.7) * mm});
            skLineSegment(sketch, "E1.11.1.0", {"start": v(157.16, 14.29) * mm, "end": v(169.86, 14.29) * mm});
            skLineSegment(sketch, "E1.11.1.1", {"start": v(157.16, 26.99) * mm, "end": v(169.86, 26.99) * mm});
            skLineSegment(sketch, "E1.11.1.2", {"start": v(157.16, 14.29) * mm, "end": v(157.16, 26.99) * mm});
            skLineSegment(sketch, "E1.11.1.3", {"start": v(169.86, 14.29) * mm, "end": v(169.86, 26.99) * mm});
            skLineSegment(sketch, "E1.11.2.0", {"start": v(157.16, 28.58) * mm, "end": v(169.86, 28.58) * mm});
            skLineSegment(sketch, "E1.11.2.1", {"start": v(157.16, 41.28) * mm, "end": v(169.86, 41.28) * mm});
            skLineSegment(sketch, "E1.11.2.2", {"start": v(157.16, 28.57) * mm, "end": v(157.16, 41.27) * mm});
            skLineSegment(sketch, "E1.11.2.3", {"start": v(169.86, 28.57) * mm, "end": v(169.86, 41.27) * mm});
            skLineSegment(sketch, "E1.11.3.0", {"start": v(157.16, 42.86) * mm, "end": v(169.86, 42.86) * mm});
            skLineSegment(sketch, "E1.11.3.1", {"start": v(157.16, 55.56) * mm, "end": v(169.86, 55.56) * mm});
            skLineSegment(sketch, "E1.11.3.2", {"start": v(157.16, 42.86) * mm, "end": v(157.16, 55.56) * mm});
            skLineSegment(sketch, "E1.11.3.3", {"start": v(169.86, 42.86) * mm, "end": v(169.86, 55.56) * mm});
            skLineSegment(sketch, "E1.11.4.0", {"start": v(157.16, 57.15) * mm, "end": v(169.86, 57.15) * mm});
            skLineSegment(sketch, "E1.11.4.1", {"start": v(157.16, 69.85) * mm, "end": v(169.86, 69.85) * mm});
            skLineSegment(sketch, "E1.11.4.2", {"start": v(157.16, 57.15) * mm, "end": v(157.16, 69.85) * mm});
            skLineSegment(sketch, "E1.11.4.3", {"start": v(169.86, 57.15) * mm, "end": v(169.86, 69.85) * mm});
            skLineSegment(sketch, "E1.11.5.0", {"start": v(157.16, 71.44) * mm, "end": v(169.86, 71.44) * mm});
            skLineSegment(sketch, "E1.11.5.1", {"start": v(157.16, 84.14) * mm, "end": v(169.86, 84.14) * mm});
            skLineSegment(sketch, "E1.11.5.2", {"start": v(157.16, 71.44) * mm, "end": v(157.16, 84.14) * mm});
            skLineSegment(sketch, "E1.11.5.3", {"start": v(169.86, 71.44) * mm, "end": v(169.86, 84.14) * mm});
            skLineSegment(sketch, "E1.11.6.0", {"start": v(157.16, 85.73) * mm, "end": v(169.86, 85.73) * mm});
            skLineSegment(sketch, "E1.11.6.1", {"start": v(157.16, 98.43) * mm, "end": v(169.86, 98.43) * mm});
            skLineSegment(sketch, "E1.11.6.2", {"start": v(157.16, 85.73) * mm, "end": v(157.16, 98.43) * mm});
            skLineSegment(sketch, "E1.11.6.3", {"start": v(169.86, 85.73) * mm, "end": v(169.86, 98.43) * mm});
            skLineSegment(sketch, "E1.11.7.0", {"start": v(157.16, 100.01) * mm, "end": v(169.86, 100.01) * mm});
            skLineSegment(sketch, "E1.11.7.1", {"start": v(157.16, 112.71) * mm, "end": v(169.86, 112.71) * mm});
            skLineSegment(sketch, "E1.11.7.2", {"start": v(157.16, 100.01) * mm, "end": v(157.16, 112.71) * mm});
            skLineSegment(sketch, "E1.11.7.3", {"start": v(169.86, 100.01) * mm, "end": v(169.86, 112.71) * mm});
            skLineSegment(sketch, "E1.12.0.0", {"start": v(171.45, 0) * mm, "end": v(184.15, 0) * mm});
            skLineSegment(sketch, "E1.12.0.1", {"start": v(171.45, 12.7) * mm, "end": v(184.15, 12.7) * mm});
            skLineSegment(sketch, "E1.12.0.2", {"start": v(171.45, 0) * mm, "end": v(171.45, 12.7) * mm});
            skLineSegment(sketch, "E1.12.0.3", {"start": v(184.15, 0) * mm, "end": v(184.15, 12.7) * mm});
            skLineSegment(sketch, "E1.12.1.0", {"start": v(171.45, 14.29) * mm, "end": v(184.15, 14.29) * mm});
            skLineSegment(sketch, "E1.12.1.1", {"start": v(171.45, 26.99) * mm, "end": v(184.15, 26.99) * mm});
            skLineSegment(sketch, "E1.12.1.2", {"start": v(171.45, 14.29) * mm, "end": v(171.45, 26.99) * mm});
            skLineSegment(sketch, "E1.12.1.3", {"start": v(184.15, 14.29) * mm, "end": v(184.15, 26.99) * mm});
            skLineSegment(sketch, "E1.12.2.0", {"start": v(171.45, 28.58) * mm, "end": v(184.15, 28.58) * mm});
            skLineSegment(sketch, "E1.12.2.1", {"start": v(171.45, 41.28) * mm, "end": v(184.15, 41.28) * mm});
            skLineSegment(sketch, "E1.12.2.2", {"start": v(171.45, 28.57) * mm, "end": v(171.45, 41.27) * mm});
            skLineSegment(sketch, "E1.12.2.3", {"start": v(184.15, 28.57) * mm, "end": v(184.15, 41.27) * mm});
            skLineSegment(sketch, "E1.12.3.0", {"start": v(171.45, 42.86) * mm, "end": v(184.15, 42.86) * mm});
            skLineSegment(sketch, "E1.12.3.1", {"start": v(171.45, 55.56) * mm, "end": v(184.15, 55.56) * mm});
            skLineSegment(sketch, "E1.12.3.2", {"start": v(171.45, 42.86) * mm, "end": v(171.45, 55.56) * mm});
            skLineSegment(sketch, "E1.12.3.3", {"start": v(184.15, 42.86) * mm, "end": v(184.15, 55.56) * mm});
            skLineSegment(sketch, "E1.12.4.0", {"start": v(171.45, 57.15) * mm, "end": v(184.15, 57.15) * mm});
            skLineSegment(sketch, "E1.12.4.1", {"start": v(171.45, 69.85) * mm, "end": v(184.15, 69.85) * mm});
            skLineSegment(sketch, "E1.12.4.2", {"start": v(171.45, 57.15) * mm, "end": v(171.45, 69.85) * mm});
            skLineSegment(sketch, "E1.12.4.3", {"start": v(184.15, 57.15) * mm, "end": v(184.15, 69.85) * mm});
            skLineSegment(sketch, "E1.12.5.0", {"start": v(171.45, 71.44) * mm, "end": v(184.15, 71.44) * mm});
            skLineSegment(sketch, "E1.12.5.1", {"start": v(171.45, 84.14) * mm, "end": v(184.15, 84.14) * mm});
            skLineSegment(sketch, "E1.12.5.2", {"start": v(171.45, 71.44) * mm, "end": v(171.45, 84.14) * mm});
            skLineSegment(sketch, "E1.12.5.3", {"start": v(184.15, 71.44) * mm, "end": v(184.15, 84.14) * mm});
            skLineSegment(sketch, "E1.12.6.0", {"start": v(171.45, 85.73) * mm, "end": v(184.15, 85.73) * mm});
            skLineSegment(sketch, "E1.12.6.1", {"start": v(171.45, 98.43) * mm, "end": v(184.15, 98.43) * mm});
            skLineSegment(sketch, "E1.12.6.2", {"start": v(171.45, 85.73) * mm, "end": v(171.45, 98.43) * mm});
            skLineSegment(sketch, "E1.12.6.3", {"start": v(184.15, 85.73) * mm, "end": v(184.15, 98.43) * mm});
            skLineSegment(sketch, "E1.12.7.0", {"start": v(171.45, 100.01) * mm, "end": v(184.15, 100.01) * mm});
            skLineSegment(sketch, "E1.12.7.1", {"start": v(171.45, 112.71) * mm, "end": v(184.15, 112.71) * mm});
            skLineSegment(sketch, "E1.12.7.2", {"start": v(171.45, 100.01) * mm, "end": v(171.45, 112.71) * mm});
            skLineSegment(sketch, "E1.12.7.3", {"start": v(184.15, 100.01) * mm, "end": v(184.15, 112.71) * mm});
            skLineSegment(sketch, "E1.13.0.0", {"start": v(185.74, 0) * mm, "end": v(198.44, 0) * mm});
            skLineSegment(sketch, "E1.13.0.1", {"start": v(185.74, 12.7) * mm, "end": v(198.44, 12.7) * mm});
            skLineSegment(sketch, "E1.13.0.2", {"start": v(185.74, 0) * mm, "end": v(185.74, 12.7) * mm});
            skLineSegment(sketch, "E1.13.0.3", {"start": v(198.44, 0) * mm, "end": v(198.44, 12.7) * mm});
            skLineSegment(sketch, "E1.13.1.0", {"start": v(185.74, 14.29) * mm, "end": v(198.44, 14.29) * mm});
            skLineSegment(sketch, "E1.13.1.1", {"start": v(185.74, 26.99) * mm, "end": v(198.44, 26.99) * mm});
            skLineSegment(sketch, "E1.13.1.2", {"start": v(185.74, 14.29) * mm, "end": v(185.74, 26.99) * mm});
            skLineSegment(sketch, "E1.13.1.3", {"start": v(198.44, 14.29) * mm, "end": v(198.44, 26.99) * mm});
            skLineSegment(sketch, "E1.13.2.0", {"start": v(185.74, 28.58) * mm, "end": v(198.44, 28.58) * mm});
            skLineSegment(sketch, "E1.13.2.1", {"start": v(185.74, 41.28) * mm, "end": v(198.44, 41.28) * mm});
            skLineSegment(sketch, "E1.13.2.2", {"start": v(185.74, 28.57) * mm, "end": v(185.74, 41.27) * mm});
            skLineSegment(sketch, "E1.13.2.3", {"start": v(198.44, 28.57) * mm, "end": v(198.44, 41.27) * mm});
            skLineSegment(sketch, "E1.13.3.0", {"start": v(185.74, 42.86) * mm, "end": v(198.44, 42.86) * mm});
            skLineSegment(sketch, "E1.13.3.1", {"start": v(185.74, 55.56) * mm, "end": v(198.44, 55.56) * mm});
            skLineSegment(sketch, "E1.13.3.2", {"start": v(185.74, 42.86) * mm, "end": v(185.74, 55.56) * mm});
            skLineSegment(sketch, "E1.13.3.3", {"start": v(198.44, 42.86) * mm, "end": v(198.44, 55.56) * mm});
            skLineSegment(sketch, "E1.13.4.0", {"start": v(185.74, 57.15) * mm, "end": v(198.44, 57.15) * mm});
            skLineSegment(sketch, "E1.13.4.1", {"start": v(185.74, 69.85) * mm, "end": v(198.44, 69.85) * mm});
            skLineSegment(sketch, "E1.13.4.2", {"start": v(185.74, 57.15) * mm, "end": v(185.74, 69.85) * mm});
            skLineSegment(sketch, "E1.13.4.3", {"start": v(198.44, 57.15) * mm, "end": v(198.44, 69.85) * mm});
            skLineSegment(sketch, "E1.13.5.0", {"start": v(185.74, 71.44) * mm, "end": v(198.44, 71.44) * mm});
            skLineSegment(sketch, "E1.13.5.1", {"start": v(185.74, 84.14) * mm, "end": v(198.44, 84.14) * mm});
            skLineSegment(sketch, "E1.13.5.2", {"start": v(185.74, 71.44) * mm, "end": v(185.74, 84.14) * mm});
            skLineSegment(sketch, "E1.13.5.3", {"start": v(198.44, 71.44) * mm, "end": v(198.44, 84.14) * mm});
            skLineSegment(sketch, "E1.13.6.0", {"start": v(185.74, 85.73) * mm, "end": v(198.44, 85.73) * mm});
            skLineSegment(sketch, "E1.13.6.1", {"start": v(185.74, 98.43) * mm, "end": v(198.44, 98.43) * mm});
            skLineSegment(sketch, "E1.13.6.2", {"start": v(185.74, 85.73) * mm, "end": v(185.74, 98.43) * mm});
            skLineSegment(sketch, "E1.13.6.3", {"start": v(198.44, 85.73) * mm, "end": v(198.44, 98.43) * mm});
            skLineSegment(sketch, "E1.13.7.0", {"start": v(185.74, 100.01) * mm, "end": v(198.44, 100.01) * mm});
            skLineSegment(sketch, "E1.13.7.1", {"start": v(185.74, 112.71) * mm, "end": v(198.44, 112.71) * mm});
            skLineSegment(sketch, "E1.13.7.2", {"start": v(185.74, 100.01) * mm, "end": v(185.74, 112.71) * mm});
            skLineSegment(sketch, "E1.13.7.3", {"start": v(198.44, 100.01) * mm, "end": v(198.44, 112.71) * mm});
            skLineSegment(sketch, "E1.14.0.0", {"start": v(200.03, 0) * mm, "end": v(212.72, 0) * mm});
            skLineSegment(sketch, "E1.14.0.1", {"start": v(200.03, 12.7) * mm, "end": v(212.72, 12.7) * mm});
            skLineSegment(sketch, "E1.14.0.2", {"start": v(200.03, 0) * mm, "end": v(200.03, 12.7) * mm});
            skLineSegment(sketch, "E1.14.0.3", {"start": v(212.72, 0) * mm, "end": v(212.72, 12.7) * mm});
            skLineSegment(sketch, "E1.14.1.0", {"start": v(200.03, 14.29) * mm, "end": v(212.72, 14.29) * mm});
            skLineSegment(sketch, "E1.14.1.1", {"start": v(200.03, 26.99) * mm, "end": v(212.72, 26.99) * mm});
            skLineSegment(sketch, "E1.14.1.2", {"start": v(200.03, 14.29) * mm, "end": v(200.03, 26.99) * mm});
            skLineSegment(sketch, "E1.14.1.3", {"start": v(212.72, 14.29) * mm, "end": v(212.72, 26.99) * mm});
            skLineSegment(sketch, "E1.14.2.0", {"start": v(200.03, 28.58) * mm, "end": v(212.72, 28.58) * mm});
            skLineSegment(sketch, "E1.14.2.1", {"start": v(200.03, 41.28) * mm, "end": v(212.72, 41.28) * mm});
            skLineSegment(sketch, "E1.14.2.2", {"start": v(200.03, 28.57) * mm, "end": v(200.03, 41.27) * mm});
            skLineSegment(sketch, "E1.14.2.3", {"start": v(212.72, 28.57) * mm, "end": v(212.72, 41.27) * mm});
            skLineSegment(sketch, "E1.14.3.0", {"start": v(200.03, 42.86) * mm, "end": v(212.72, 42.86) * mm});
            skLineSegment(sketch, "E1.14.3.1", {"start": v(200.03, 55.56) * mm, "end": v(212.72, 55.56) * mm});
            skLineSegment(sketch, "E1.14.3.2", {"start": v(200.03, 42.86) * mm, "end": v(200.03, 55.56) * mm});
            skLineSegment(sketch, "E1.14.3.3", {"start": v(212.72, 42.86) * mm, "end": v(212.72, 55.56) * mm});
            skLineSegment(sketch, "E1.14.4.0", {"start": v(200.03, 57.15) * mm, "end": v(212.72, 57.15) * mm});
            skLineSegment(sketch, "E1.14.4.1", {"start": v(200.03, 69.85) * mm, "end": v(212.72, 69.85) * mm});
            skLineSegment(sketch, "E1.14.4.2", {"start": v(200.03, 57.15) * mm, "end": v(200.03, 69.85) * mm});
            skLineSegment(sketch, "E1.14.4.3", {"start": v(212.72, 57.15) * mm, "end": v(212.72, 69.85) * mm});
            skLineSegment(sketch, "E1.14.5.0", {"start": v(200.03, 71.44) * mm, "end": v(212.72, 71.44) * mm});
            skLineSegment(sketch, "E1.14.5.1", {"start": v(200.03, 84.14) * mm, "end": v(212.72, 84.14) * mm});
            skLineSegment(sketch, "E1.14.5.2", {"start": v(200.03, 71.44) * mm, "end": v(200.03, 84.14) * mm});
            skLineSegment(sketch, "E1.14.5.3", {"start": v(212.72, 71.44) * mm, "end": v(212.72, 84.14) * mm});
            skLineSegment(sketch, "E1.14.6.0", {"start": v(200.03, 85.73) * mm, "end": v(212.72, 85.73) * mm});
            skLineSegment(sketch, "E1.14.6.1", {"start": v(200.03, 98.43) * mm, "end": v(212.72, 98.43) * mm});
            skLineSegment(sketch, "E1.14.6.2", {"start": v(200.03, 85.73) * mm, "end": v(200.03, 98.43) * mm});
            skLineSegment(sketch, "E1.14.6.3", {"start": v(212.72, 85.73) * mm, "end": v(212.72, 98.43) * mm});
            skLineSegment(sketch, "E1.14.7.0", {"start": v(200.03, 100.01) * mm, "end": v(212.72, 100.01) * mm});
            skLineSegment(sketch, "E1.14.7.1", {"start": v(200.03, 112.71) * mm, "end": v(212.72, 112.71) * mm});
            skLineSegment(sketch, "E1.14.7.2", {"start": v(200.03, 100.01) * mm, "end": v(200.03, 112.71) * mm});
            skLineSegment(sketch, "E1.14.7.3", {"start": v(212.72, 100.01) * mm, "end": v(212.72, 112.71) * mm});
            skLineSegment(sketch, "E1.15.0.0", {"start": v(214.31, 0) * mm, "end": v(227.01, 0) * mm});
            skLineSegment(sketch, "E1.15.0.1", {"start": v(214.31, 12.7) * mm, "end": v(227.01, 12.7) * mm});
            skLineSegment(sketch, "E1.15.0.2", {"start": v(214.31, 0) * mm, "end": v(214.31, 12.7) * mm});
            skLineSegment(sketch, "E1.15.0.3", {"start": v(227.01, 0) * mm, "end": v(227.01, 12.7) * mm});
            skLineSegment(sketch, "E1.15.1.0", {"start": v(214.31, 14.29) * mm, "end": v(227.01, 14.29) * mm});
            skLineSegment(sketch, "E1.15.1.1", {"start": v(214.31, 26.99) * mm, "end": v(227.01, 26.99) * mm});
            skLineSegment(sketch, "E1.15.1.2", {"start": v(214.31, 14.29) * mm, "end": v(214.31, 26.99) * mm});
            skLineSegment(sketch, "E1.15.1.3", {"start": v(227.01, 14.29) * mm, "end": v(227.01, 26.99) * mm});
            skLineSegment(sketch, "E1.15.2.0", {"start": v(214.31, 28.58) * mm, "end": v(227.01, 28.58) * mm});
            skLineSegment(sketch, "E1.15.2.1", {"start": v(214.31, 41.28) * mm, "end": v(227.01, 41.28) * mm});
            skLineSegment(sketch, "E1.15.2.2", {"start": v(214.31, 28.57) * mm, "end": v(214.31, 41.27) * mm});
            skLineSegment(sketch, "E1.15.2.3", {"start": v(227.01, 28.57) * mm, "end": v(227.01, 41.27) * mm});
            skLineSegment(sketch, "E1.15.3.0", {"start": v(214.31, 42.86) * mm, "end": v(227.01, 42.86) * mm});
            skLineSegment(sketch, "E1.15.3.1", {"start": v(214.31, 55.56) * mm, "end": v(227.01, 55.56) * mm});
            skLineSegment(sketch, "E1.15.3.2", {"start": v(214.31, 42.86) * mm, "end": v(214.31, 55.56) * mm});
            skLineSegment(sketch, "E1.15.3.3", {"start": v(227.01, 42.86) * mm, "end": v(227.01, 55.56) * mm});
            skLineSegment(sketch, "E1.15.4.0", {"start": v(214.31, 57.15) * mm, "end": v(227.01, 57.15) * mm});
            skLineSegment(sketch, "E1.15.4.1", {"start": v(214.31, 69.85) * mm, "end": v(227.01, 69.85) * mm});
            skLineSegment(sketch, "E1.15.4.2", {"start": v(214.31, 57.15) * mm, "end": v(214.31, 69.85) * mm});
            skLineSegment(sketch, "E1.15.4.3", {"start": v(227.01, 57.15) * mm, "end": v(227.01, 69.85) * mm});
            skLineSegment(sketch, "E1.15.5.0", {"start": v(214.31, 71.44) * mm, "end": v(227.01, 71.44) * mm});
            skLineSegment(sketch, "E1.15.5.1", {"start": v(214.31, 84.14) * mm, "end": v(227.01, 84.14) * mm});
            skLineSegment(sketch, "E1.15.5.2", {"start": v(214.31, 71.44) * mm, "end": v(214.31, 84.14) * mm});
            skLineSegment(sketch, "E1.15.5.3", {"start": v(227.01, 71.44) * mm, "end": v(227.01, 84.14) * mm});
            skLineSegment(sketch, "E1.15.6.0", {"start": v(214.31, 85.73) * mm, "end": v(227.01, 85.73) * mm});
            skLineSegment(sketch, "E1.15.6.1", {"start": v(214.31, 98.43) * mm, "end": v(227.01, 98.43) * mm});
            skLineSegment(sketch, "E1.15.6.2", {"start": v(214.31, 85.73) * mm, "end": v(214.31, 98.43) * mm});
            skLineSegment(sketch, "E1.15.6.3", {"start": v(227.01, 85.73) * mm, "end": v(227.01, 98.43) * mm});
            skLineSegment(sketch, "E1.15.7.0", {"start": v(214.31, 100.01) * mm, "end": v(227.01, 100.01) * mm});
            skLineSegment(sketch, "E1.15.7.1", {"start": v(214.31, 112.71) * mm, "end": v(227.01, 112.71) * mm});
            skLineSegment(sketch, "E1.15.7.2", {"start": v(214.31, 100.01) * mm, "end": v(214.31, 112.71) * mm});
            skLineSegment(sketch, "E1.15.7.3", {"start": v(227.01, 100.01) * mm, "end": v(227.01, 112.71) * mm});
            skLineSegment(sketch, "E1.16.0.0", {"start": v(228.6, 0) * mm, "end": v(241.3, 0) * mm});
            skLineSegment(sketch, "E1.16.0.1", {"start": v(228.6, 12.7) * mm, "end": v(241.3, 12.7) * mm});
            skLineSegment(sketch, "E1.16.0.2", {"start": v(228.6, 0) * mm, "end": v(228.6, 12.7) * mm});
            skLineSegment(sketch, "E1.16.0.3", {"start": v(241.3, 0) * mm, "end": v(241.3, 12.7) * mm});
            skLineSegment(sketch, "E1.16.1.0", {"start": v(228.6, 14.29) * mm, "end": v(241.3, 14.29) * mm});
            skLineSegment(sketch, "E1.16.1.1", {"start": v(228.6, 26.99) * mm, "end": v(241.3, 26.99) * mm});
            skLineSegment(sketch, "E1.16.1.2", {"start": v(228.6, 14.29) * mm, "end": v(228.6, 26.99) * mm});
            skLineSegment(sketch, "E1.16.1.3", {"start": v(241.3, 14.29) * mm, "end": v(241.3, 26.99) * mm});
            skLineSegment(sketch, "E1.16.2.0", {"start": v(228.6, 28.58) * mm, "end": v(241.3, 28.58) * mm});
            skLineSegment(sketch, "E1.16.2.1", {"start": v(228.6, 41.28) * mm, "end": v(241.3, 41.28) * mm});
            skLineSegment(sketch, "E1.16.2.2", {"start": v(228.6, 28.57) * mm, "end": v(228.6, 41.27) * mm});
            skLineSegment(sketch, "E1.16.2.3", {"start": v(241.3, 28.57) * mm, "end": v(241.3, 41.27) * mm});
            skLineSegment(sketch, "E1.16.3.0", {"start": v(228.6, 42.86) * mm, "end": v(241.3, 42.86) * mm});
            skLineSegment(sketch, "E1.16.3.1", {"start": v(228.6, 55.56) * mm, "end": v(241.3, 55.56) * mm});
            skLineSegment(sketch, "E1.16.3.2", {"start": v(228.6, 42.86) * mm, "end": v(228.6, 55.56) * mm});
            skLineSegment(sketch, "E1.16.3.3", {"start": v(241.3, 42.86) * mm, "end": v(241.3, 55.56) * mm});
            skLineSegment(sketch, "E1.16.4.0", {"start": v(228.6, 57.15) * mm, "end": v(241.3, 57.15) * mm});
            skLineSegment(sketch, "E1.16.4.1", {"start": v(228.6, 69.85) * mm, "end": v(241.3, 69.85) * mm});
            skLineSegment(sketch, "E1.16.4.2", {"start": v(228.6, 57.15) * mm, "end": v(228.6, 69.85) * mm});
            skLineSegment(sketch, "E1.16.4.3", {"start": v(241.3, 57.15) * mm, "end": v(241.3, 69.85) * mm});
            skLineSegment(sketch, "E1.16.5.0", {"start": v(228.6, 71.44) * mm, "end": v(241.3, 71.44) * mm});
            skLineSegment(sketch, "E1.16.5.1", {"start": v(228.6, 84.14) * mm, "end": v(241.3, 84.14) * mm});
            skLineSegment(sketch, "E1.16.5.2", {"start": v(228.6, 71.44) * mm, "end": v(228.6, 84.14) * mm});
            skLineSegment(sketch, "E1.16.5.3", {"start": v(241.3, 71.44) * mm, "end": v(241.3, 84.14) * mm});
            skLineSegment(sketch, "E1.16.6.0", {"start": v(228.6, 85.73) * mm, "end": v(241.3, 85.73) * mm});
            skLineSegment(sketch, "E1.16.6.1", {"start": v(228.6, 98.43) * mm, "end": v(241.3, 98.43) * mm});
            skLineSegment(sketch, "E1.16.6.2", {"start": v(228.6, 85.73) * mm, "end": v(228.6, 98.43) * mm});
            skLineSegment(sketch, "E1.16.6.3", {"start": v(241.3, 85.73) * mm, "end": v(241.3, 98.43) * mm});
            skLineSegment(sketch, "E1.16.7.0", {"start": v(228.6, 100.01) * mm, "end": v(241.3, 100.01) * mm});
            skLineSegment(sketch, "E1.16.7.1", {"start": v(228.6, 112.71) * mm, "end": v(241.3, 112.71) * mm});
            skLineSegment(sketch, "E1.16.7.2", {"start": v(228.6, 100.01) * mm, "end": v(228.6, 112.71) * mm});
            skLineSegment(sketch, "E1.16.7.3", {"start": v(241.3, 100.01) * mm, "end": v(241.3, 112.71) * mm});
            skLineSegment(sketch, "E1.17.0.0", {"start": v(242.89, 0) * mm, "end": v(255.59, 0) * mm});
            skLineSegment(sketch, "E1.17.0.1", {"start": v(242.89, 12.7) * mm, "end": v(255.59, 12.7) * mm});
            skLineSegment(sketch, "E1.17.0.2", {"start": v(242.89, 0) * mm, "end": v(242.89, 12.7) * mm});
            skLineSegment(sketch, "E1.17.0.3", {"start": v(255.59, 0) * mm, "end": v(255.59, 12.7) * mm});
            skLineSegment(sketch, "E1.17.1.0", {"start": v(242.89, 14.29) * mm, "end": v(255.59, 14.29) * mm});
            skLineSegment(sketch, "E1.17.1.1", {"start": v(242.89, 26.99) * mm, "end": v(255.59, 26.99) * mm});
            skLineSegment(sketch, "E1.17.1.2", {"start": v(242.89, 14.29) * mm, "end": v(242.89, 26.99) * mm});
            skLineSegment(sketch, "E1.17.1.3", {"start": v(255.59, 14.29) * mm, "end": v(255.59, 26.99) * mm});
            skLineSegment(sketch, "E1.17.2.0", {"start": v(242.89, 28.58) * mm, "end": v(255.59, 28.58) * mm});
            skLineSegment(sketch, "E1.17.2.1", {"start": v(242.89, 41.28) * mm, "end": v(255.59, 41.28) * mm});
            skLineSegment(sketch, "E1.17.2.2", {"start": v(242.89, 28.57) * mm, "end": v(242.89, 41.27) * mm});
            skLineSegment(sketch, "E1.17.2.3", {"start": v(255.59, 28.57) * mm, "end": v(255.59, 41.27) * mm});
            skLineSegment(sketch, "E1.17.3.0", {"start": v(242.89, 42.86) * mm, "end": v(255.59, 42.86) * mm});
            skLineSegment(sketch, "E1.17.3.1", {"start": v(242.89, 55.56) * mm, "end": v(255.59, 55.56) * mm});
            skLineSegment(sketch, "E1.17.3.2", {"start": v(242.89, 42.86) * mm, "end": v(242.89, 55.56) * mm});
            skLineSegment(sketch, "E1.17.3.3", {"start": v(255.59, 42.86) * mm, "end": v(255.59, 55.56) * mm});
            skLineSegment(sketch, "E1.17.4.0", {"start": v(242.89, 57.15) * mm, "end": v(255.59, 57.15) * mm});
            skLineSegment(sketch, "E1.17.4.1", {"start": v(242.89, 69.85) * mm, "end": v(255.59, 69.85) * mm});
            skLineSegment(sketch, "E1.17.4.2", {"start": v(242.89, 57.15) * mm, "end": v(242.89, 69.85) * mm});
            skLineSegment(sketch, "E1.17.4.3", {"start": v(255.59, 57.15) * mm, "end": v(255.59, 69.85) * mm});
            skLineSegment(sketch, "E1.17.5.0", {"start": v(242.89, 71.44) * mm, "end": v(255.59, 71.44) * mm});
            skLineSegment(sketch, "E1.17.5.1", {"start": v(242.89, 84.14) * mm, "end": v(255.59, 84.14) * mm});
            skLineSegment(sketch, "E1.17.5.2", {"start": v(242.89, 71.44) * mm, "end": v(242.89, 84.14) * mm});
            skLineSegment(sketch, "E1.17.5.3", {"start": v(255.59, 71.44) * mm, "end": v(255.59, 84.14) * mm});
            skLineSegment(sketch, "E1.17.6.0", {"start": v(242.89, 85.73) * mm, "end": v(255.59, 85.73) * mm});
            skLineSegment(sketch, "E1.17.6.1", {"start": v(242.89, 98.43) * mm, "end": v(255.59, 98.43) * mm});
            skLineSegment(sketch, "E1.17.6.2", {"start": v(242.89, 85.73) * mm, "end": v(242.89, 98.43) * mm});
            skLineSegment(sketch, "E1.17.6.3", {"start": v(255.59, 85.73) * mm, "end": v(255.59, 98.43) * mm});
            skLineSegment(sketch, "E1.17.7.0", {"start": v(242.89, 100.01) * mm, "end": v(255.59, 100.01) * mm});
            skLineSegment(sketch, "E1.17.7.1", {"start": v(242.89, 112.71) * mm, "end": v(255.59, 112.71) * mm});
            skLineSegment(sketch, "E1.17.7.2", {"start": v(242.89, 100.01) * mm, "end": v(242.89, 112.71) * mm});
            skLineSegment(sketch, "E1.17.7.3", {"start": v(255.59, 100.01) * mm, "end": v(255.59, 112.71) * mm});
            skLineSegment(sketch, "E1.direction1", {"start": v(0, 0) * mm, "end": v(14.29, 0) * mm, "construction": true});
            skLineSegment(sketch, "E1.direction2", {"start": v(0, 0) * mm, "end": v(0, 14.29) * mm, "construction": true});
            skLineSegment(sketch, "E2.bottom", {"start": v(-1.59, 114.3) * mm, "end": v(257.18, 114.3) * mm});
            skLineSegment(sketch, "E2.top", {"start": v(-1.59, -1.59) * mm, "end": v(257.18, -1.59) * mm});
            skLineSegment(sketch, "E2.left", {"start": v(-1.59, 114.3) * mm, "end": v(-1.59, -1.59) * mm});
            skLineSegment(sketch, "E2.right", {"start": v(257.18, 114.3) * mm, "end": v(257.18, -1.59) * mm});
            skSolve(sketch);
        }
        {
            var Q0;
            Q0 = qSketchRegion(id + "F0", true);
            extrude(context, id + "F1", {"entities" : qUnion([Q0]), "depth" : 12.7 * mm});
        }
    });
